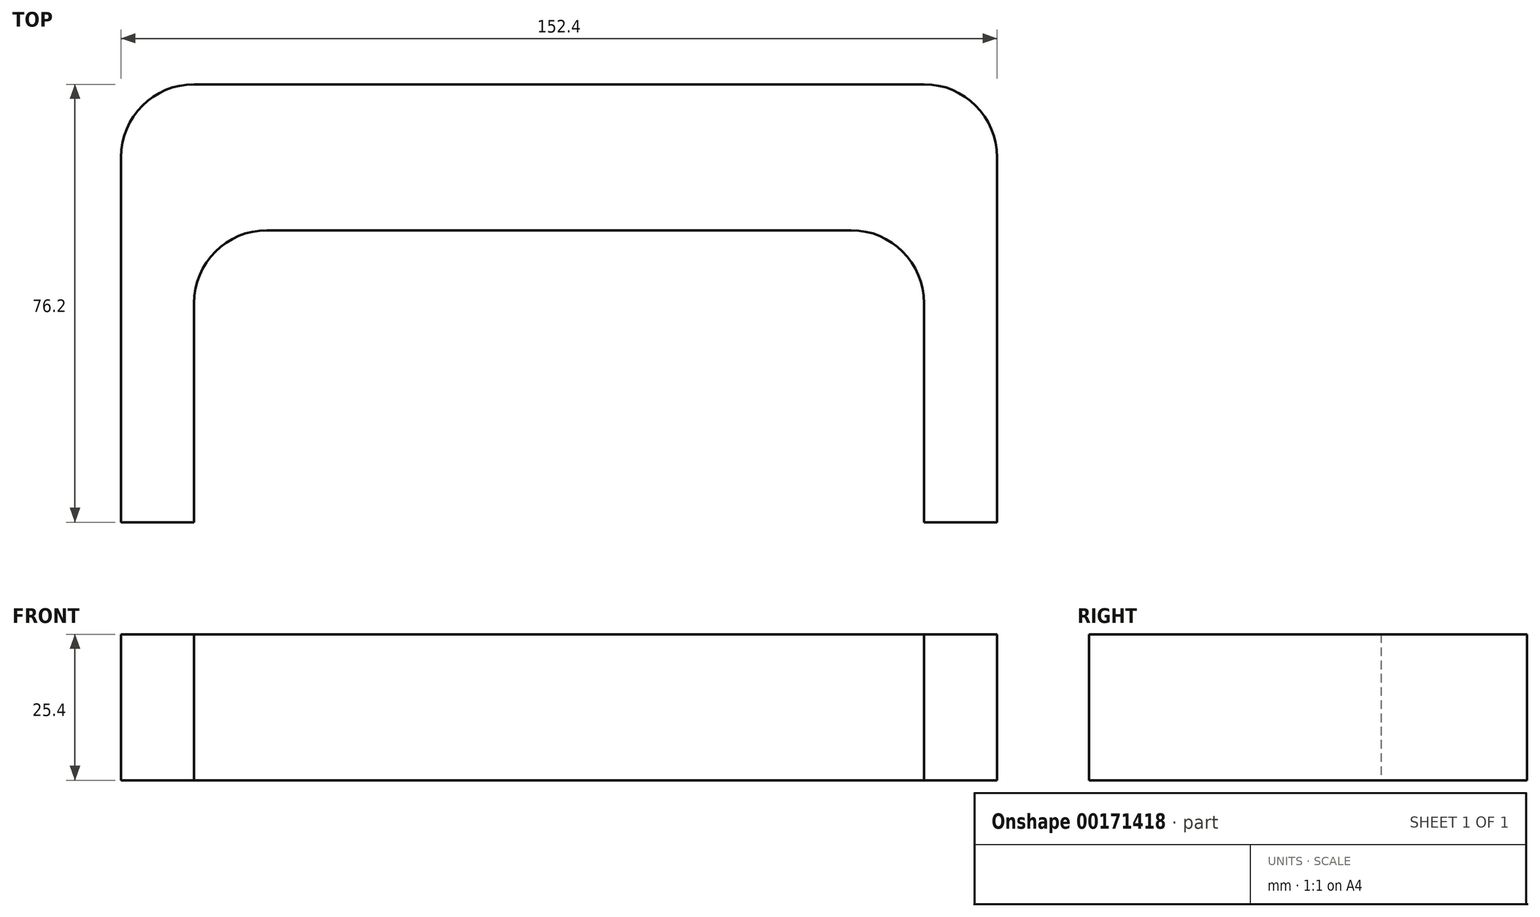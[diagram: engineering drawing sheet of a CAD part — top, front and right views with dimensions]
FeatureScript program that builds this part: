
annotation { "Feature Type Name" : "Feature", "Feature Type Description" : "" }
export const myFeature = defineFeature(function(context is Context, id is Id, definition is map)
    precondition{}
    {
        {
            var Q0;
            Q0=qCreatedBy(makeId("Top.planeOp"),FACE);
            var sketch = newSketch(context, id + "F0", { "sketchPlane" : qUnion([Q0])});
            skLineSegment(sketch, "E0", {"start": v(-135.24, 0) * mm, "end": v(-135.24, 38.1) * mm});
            skLineSegment(sketch, "E1", {"start": v(-122.54, 50.8) * mm, "end": v(-20.94, 50.8) * mm});
            skLineSegment(sketch, "E2", {"start": v(-8.24, 38.1) * mm, "end": v(-8.24, 0) * mm});
            skLineSegment(sketch, "E3", {"start": v(-147.94, 0) * mm, "end": v(-147.94, 63.5) * mm});
            skLineSegment(sketch, "E4", {"start": v(-135.24, 76.2) * mm, "end": v(-8.24, 76.2) * mm});
            skLineSegment(sketch, "E5", {"start": v(4.46, 63.5) * mm, "end": v(4.46, 0) * mm});
            skLineSegment(sketch, "E6", {"start": v(-147.94, 0) * mm, "end": v(-135.24, 0) * mm});
            skLineSegment(sketch, "E7", {"start": v(-8.24, 0) * mm, "end": v(4.46, 0) * mm});
            skPoint(sketch, "E8.visualSharp", {"position": v(-147.94, 76.2) * mm});
            skArc(sketch, "E8.filletArc", {"start": v(-135.24, 76.2) * mm, "mid": v(-144.22, 72.48) * mm, "end": v(-147.94, 63.5) * mm});
            skPoint(sketch, "E9.visualSharp", {"position": v(4.46, 76.2) * mm});
            skArc(sketch, "E9.filletArc", {"start": v(4.46, 63.5) * mm, "mid": v(0.74, 72.48) * mm, "end": v(-8.24, 76.2) * mm});
            skPoint(sketch, "E10.visualSharp", {"position": v(-135.24, 50.8) * mm});
            skArc(sketch, "E10.filletArc", {"start": v(-122.54, 50.8) * mm, "mid": v(-131.52, 47.08) * mm, "end": v(-135.24, 38.1) * mm});
            skPoint(sketch, "E11.visualSharp", {"position": v(-8.24, 50.8) * mm});
            skArc(sketch, "E11.filletArc", {"start": v(-8.24, 38.1) * mm, "mid": v(-11.96, 47.08) * mm, "end": v(-20.94, 50.8) * mm});
            skSolve(sketch);
        }
        {
            var Q0;
            Q0=makeQuery(id+"F0.imprint","IMPRINT",FACE,{"disambiguationData":[TD([[makeQuery(id+"F0.imprint","IMPRINT",EDGE,{"derivedFrom":sQuery(id+"F0.wireOp",EDGE,"E0")}),1.0]])]});
            extrude(context, id + "F1", {"entities" : qUnion([Q0]), "depth" : 25.4 * mm});
        }
    });
